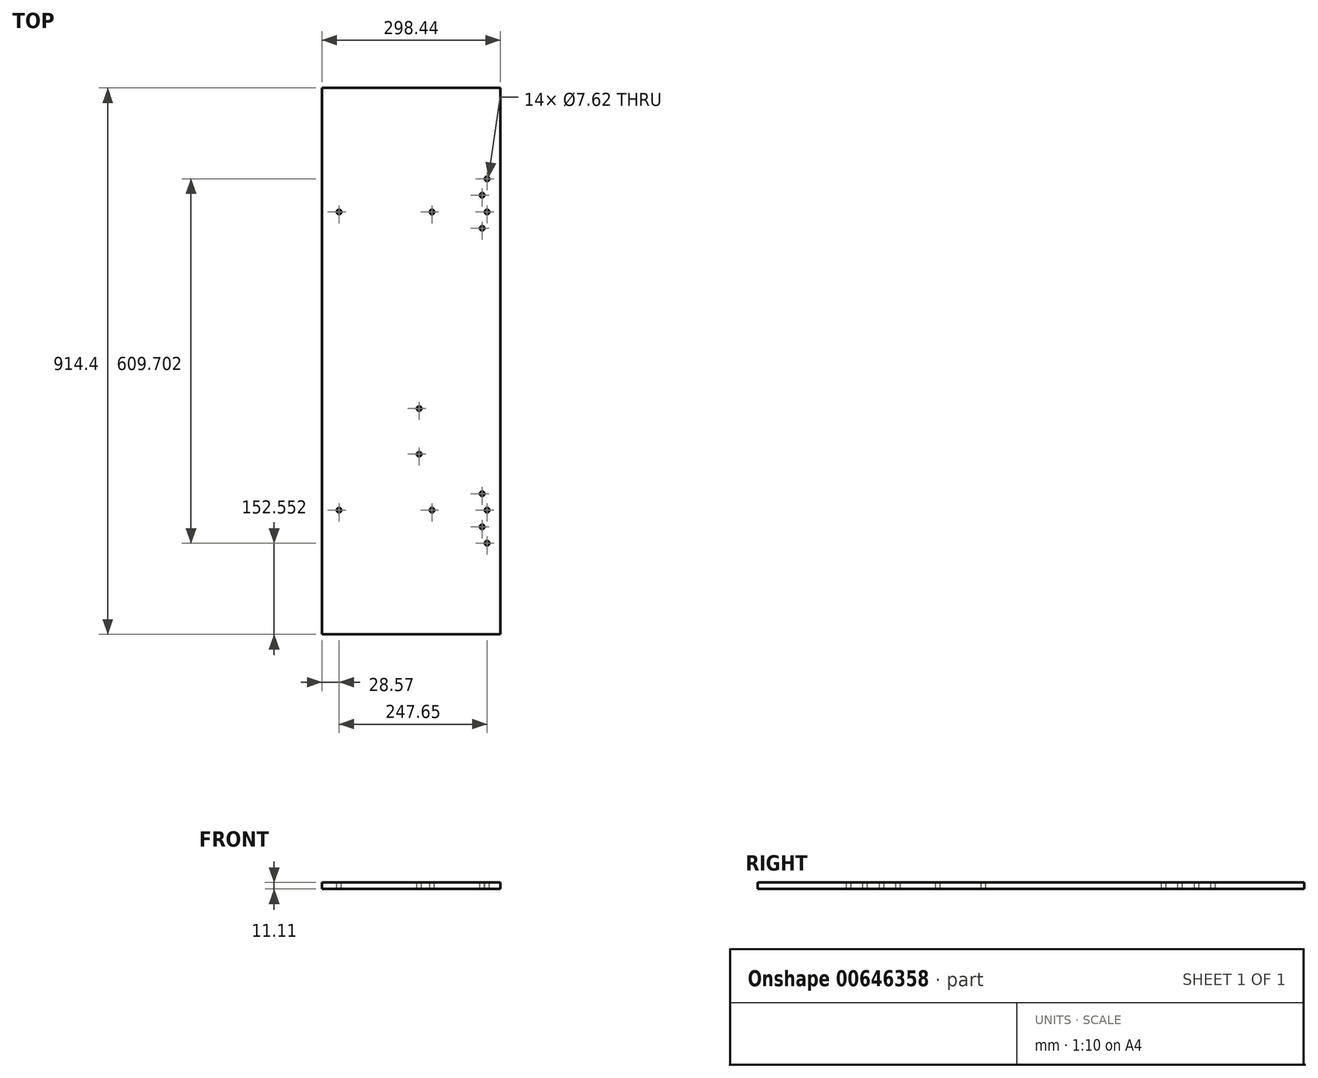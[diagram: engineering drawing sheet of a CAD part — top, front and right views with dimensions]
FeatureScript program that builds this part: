
annotation { "Feature Type Name" : "Feature", "Feature Type Description" : "" }
export const myFeature = defineFeature(function(context is Context, id is Id, definition is map)
    precondition{}
    {
        {
            var Q0;
            Q0=qCreatedBy(makeId("Top.planeOp"),FACE);
            var sketch = newSketch(context, id + "F0", { "sketchPlane" : qUnion([Q0])});
            skLineSegment(sketch, "E0.bottom", {"start": v(-149.22, 457.2) * mm, "end": v(149.23, 457.2) * mm});
            skLineSegment(sketch, "E0.top", {"start": v(-149.22, -457.2) * mm, "end": v(149.23, -457.2) * mm});
            skLineSegment(sketch, "E0.left", {"start": v(-149.22, 457.2) * mm, "end": v(-149.22, -457.2) * mm});
            skLineSegment(sketch, "E0.right", {"start": v(149.23, 457.2) * mm, "end": v(149.23, -457.2) * mm});
            skSolve(sketch);
        }
        {
            var Q0;
            Q0=makeQuery(id+"F0.imprint","IMPRINT",FACE,{"disambiguationData":[TD([[makeQuery(id+"F0.imprint","IMPRINT",EDGE,{"derivedFrom":sQuery(id+"F0.wireOp",EDGE,"E0.bottom")}),-1.0]])]});
            extrude(context, id + "F1", {"entities" : qUnion([Q0]), "depth" : 11.1 * mm, "offsetDistance" : 25.4 * mm});
        }
        {
            var Q0;
            Q0=makeQuery(id+"F1.opExtrude","CAP_FACE",FACE,{"disambiguationData":[OSD([sQuery(id+"F0.wireOp",EDGE,"E0.bottom"),sQuery(id+"F0.wireOp",EDGE,"E0.top"),sQuery(id+"F0.wireOp",EDGE,"E0.left"),sQuery(id+"F0.wireOp",EDGE,"E0.right")])],"isStart":false});
            var sketch = newSketch(context, id + "F2", { "sketchPlane" : qUnion([Q0])});
            skPoint(sketch, "E1", {"position": v(127, -304.65) * mm});
            skPoint(sketch, "E2", {"position": v(118.77, 222.31) * mm});
            skPoint(sketch, "E3", {"position": v(127, -249.28) * mm});
            skPoint(sketch, "E4", {"position": v(118.77, 277.7) * mm});
            skPoint(sketch, "E5", {"position": v(127, 305.05) * mm});
            skPoint(sketch, "E6", {"position": v(127, 249.67) * mm});
            skPoint(sketch, "E7", {"position": v(118.77, -221.9) * mm});
            skPoint(sketch, "E8", {"position": v(118.77, -277.3) * mm});
            skPoint(sketch, "E9", {"position": v(34.8, 249.67) * mm});
            skPoint(sketch, "E10", {"position": v(-120.65, 249.67) * mm});
            skPoint(sketch, "E11", {"position": v(34.8, -249.28) * mm});
            skPoint(sketch, "E12", {"position": v(-120.65, -249.28) * mm});
            skPoint(sketch, "E13", {"position": v(13.34, -155.68) * mm});
            skPoint(sketch, "E14", {"position": v(13.34, -79.35) * mm});
            skSolve(sketch);
        }
        {
            var Q0;
            Q0=sQuery(id+"F2.wireOp",VERTEX,"E1");
            var Q1;
            Q1=sQuery(id+"F2.wireOp",VERTEX,"E8");
            var Q2;
            Q2=sQuery(id+"F2.wireOp",VERTEX,"E3");
            var Q3;
            Q3=sQuery(id+"F2.wireOp",VERTEX,"E7");
            var Q4;
            Q4=sQuery(id+"F2.wireOp",VERTEX,"E2");
            var Q5;
            Q5=sQuery(id+"F2.wireOp",VERTEX,"E6");
            var Q6;
            Q6=sQuery(id+"F2.wireOp",VERTEX,"E4");
            var Q7;
            Q7=sQuery(id+"F2.wireOp",VERTEX,"E5");
            var Q8;
            Q8=sQuery(id+"F2.wireOp",VERTEX,"E9");
            var Q9;
            Q9=sQuery(id+"F2.wireOp",VERTEX,"E10");
            var Q10;
            Q10=sQuery(id+"F2.wireOp",VERTEX,"E11");
            var Q11;
            Q11=sQuery(id+"F2.wireOp",VERTEX,"E12");
            var Q12;
            Q12=sQuery(id+"F2.wireOp",VERTEX,"E13");
            var Q13;
            Q13=sQuery(id+"F2.wireOp",VERTEX,"E14");
            var Q14;
            Q14=makeQuery(id+"F1.opExtrude","SWEPT_BODY",BODY,{"disambiguationData":[OSD([sQuery(id+"F0.wireOp",EDGE,"E0.bottom"),sQuery(id+"F0.wireOp",EDGE,"E0.top"),sQuery(id+"F0.wireOp",EDGE,"E0.left"),sQuery(id+"F0.wireOp",EDGE,"E0.right")])]});
            hole(context, id + "F3", {"style" : HoleStyle.SIMPLE, "endStyle" : HoleEndStyle.BLIND, "holeDiameter" : 7.62 * mm, "majorDiameter" : 6.35 * mm, "holeDepth" : 12.7 * mm, "isTappedThrough" : true, "tappedDepth" : 12.7 * mm, "tapClearance" : 3, "locations" : qUnion([Q0, Q1, Q2, Q3, Q4, Q5, Q6, Q7, Q8, Q9, Q10, Q11, Q12, Q13]), "scope" : qUnion([Q14])});
        }
    });
